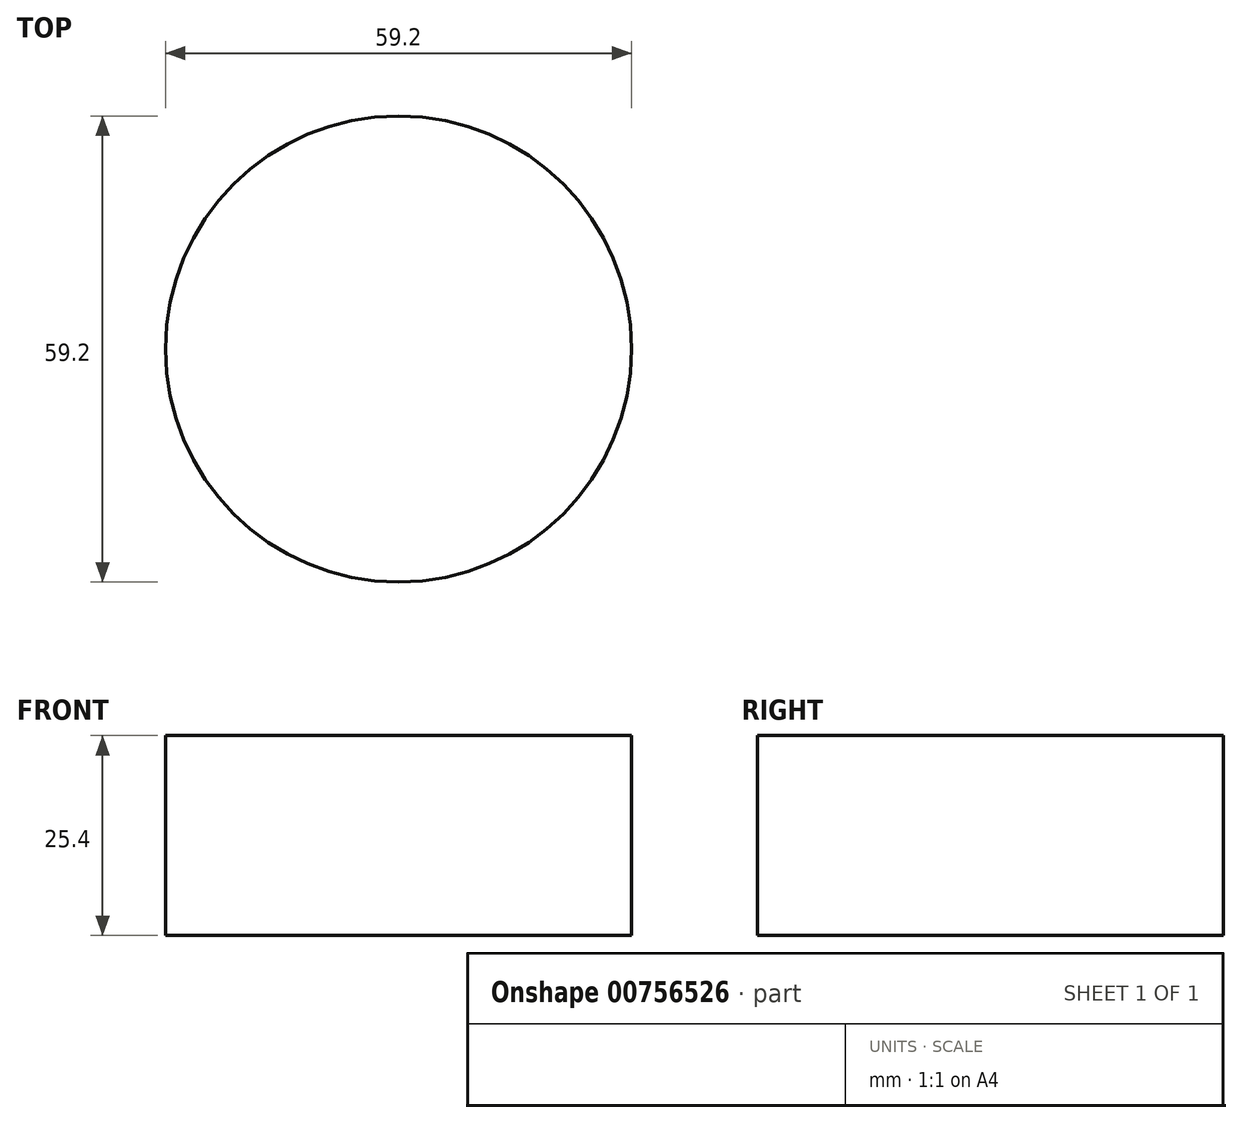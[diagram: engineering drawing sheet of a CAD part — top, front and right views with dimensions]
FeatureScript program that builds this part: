
annotation { "Feature Type Name" : "Feature", "Feature Type Description" : "" }
export const myFeature = defineFeature(function(context is Context, id is Id, definition is map)
    precondition{}
    {
        {
            var Q0;
            Q0=qCreatedBy(makeId("Top.planeOp"),FACE);
            var sketch = newSketch(context, id + "F0", { "sketchPlane" : qUnion([Q0])});
            skCircle(sketch, "E0", {"center": v(0, 0) * mm, "radius": 29.6 * mm});
            skSolve(sketch);
        }
        {
            var Q0;
            Q0 = qSketchRegion(id + "F0", true);
            extrude(context, id + "F1", {"entities" : qUnion([Q0]), "depth" : 25.4 * mm, "offsetDistance" : 25.4 * mm});
        }
    });
